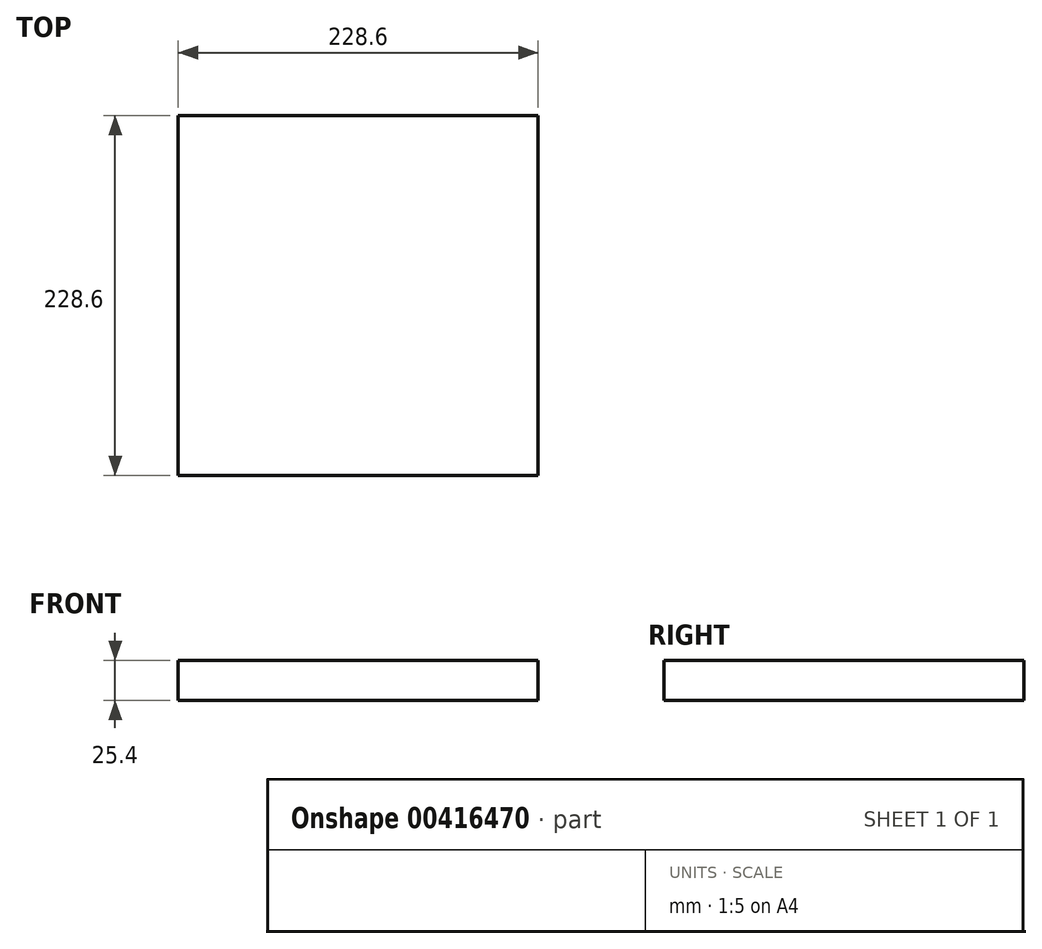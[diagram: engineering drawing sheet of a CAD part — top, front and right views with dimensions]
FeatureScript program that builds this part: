
annotation { "Feature Type Name" : "Feature", "Feature Type Description" : "" }
export const myFeature = defineFeature(function(context is Context, id is Id, definition is map)
    precondition{}
    {
        {
            var Q0;
            Q0=qCreatedBy(makeId("Top.planeOp"),FACE);
            var sketch = newSketch(context, id + "F0", { "sketchPlane" : qUnion([Q0])});
            skLineSegment(sketch, "E0", {"start": v(-304.2, -43.59) * mm, "end": v(-75.6, -43.59) * mm});
            skLineSegment(sketch, "E1", {"start": v(-75.6, -43.59) * mm, "end": v(-75.6, -272.19) * mm});
            skLineSegment(sketch, "E2", {"start": v(-75.6, -272.19) * mm, "end": v(-304.2, -272.19) * mm});
            skLineSegment(sketch, "E3", {"start": v(-304.2, -272.19) * mm, "end": v(-304.2, -43.59) * mm});
            skSolve(sketch);
        }
        {
            var Q0;
            Q0 = qSketchRegion(id + "F0", true);
            extrude(context, id + "F1", {"entities" : qUnion([Q0]), "depth" : 25.4 * mm});
        }
    });
